FCSTD DOCUMENT  (FreeCAD 0.19R0.19.2)
Label: boatMoterHolder001
License: All rights reserved
LicenseURL: http://en.wikipedia.org/wiki/All_rights_reserved
objects: Sketcher::SketchObject×1
note: 1 computed .brp shape members not serialized (recipe doc carries the construction recipe); baked Part::Feature solids carry a one-line shape summary decoded from their .brp

FEATURE [Sketcher::SketchObject] Sketch
  FullyConstrained = true
  sketch-geometry (12):
    g0: Circle CenterX=-6 CenterY=0 CenterZ=0 NormalX=0 NormalY=0 NormalZ=1 AngleXU=0 Radius=0.9
    g1: Circle CenterX=0 CenterY=6 CenterZ=0 NormalX=0 NormalY=0 NormalZ=1 AngleXU=0 Radius=0.9
    g2: Circle CenterX=6 CenterY=0 CenterZ=0 NormalX=0 NormalY=0 NormalZ=1 AngleXU=0 Radius=0.9
    g3: Circle CenterX=0 CenterY=-6 CenterZ=0 NormalX=0 NormalY=0 NormalZ=1 AngleXU=0 Radius=0.9
    g4: LineSegment StartX=0 StartY=0 StartZ=0 EndX=3.53553 EndY=-3.53553 EndZ=0
    g5: LineSegment StartX=-3.53553 StartY=-3.53553 StartZ=0 EndX=4e-16 EndY=0 EndZ=0
    g6: LineSegment StartX=3.53553 StartY=3.53553 StartZ=0 EndX=0 EndY=0 EndZ=0
    g7: LineSegment StartX=0 StartY=0 StartZ=0 EndX=-3.53553 EndY=3.53553 EndZ=0
    g8: LineSegment StartX=-7.77817 StartY=7.77817 StartZ=0 EndX=-3.53553 EndY=3.53553 EndZ=0
    g9: LineSegment StartX=3.53553 StartY=-3.53553 StartZ=0 EndX=7.77817 EndY=-7.77817 EndZ=0
    g10: LineSegment StartX=3.53553 StartY=3.53553 StartZ=0 EndX=7.77817 EndY=7.77817 EndZ=0
    g11: LineSegment StartX=-3.53553 StartY=-3.53553 StartZ=0 EndX=-7.77817 EndY=-7.77817 EndZ=0
  constraints (28):
    c: Block(g1)
    c: Block(g2)
    c: Block(g3)
    c: Block(g0)
    c: Coincident(g4,g-1)
    c: Distance(g4) = 5
    c: Angle(g4,g-1) = 0.785398
    c: Equal(g4,g5) = 5
    c: Coincident(g5,g4)
    c: Angle(g6,g-1) = 2.35619
    c: Distance(g6) = 5
    c: Coincident(g6,g4)
    c: Angle(g-1,g5) = 3.92699
    c: Coincident(g7,g4)
    c: Angle(g7,g5) = 1.5708
    c: Distance(g7) = 5
    c: Coincident(g8,g7)
    c: Distance(g8) = 6
    c: Parallel(g7,g8)
    c: Coincident(g9,g4)
    c: Distance(g9) = 6
    c: Parallel(g9,g4)
    c: Coincident(g10,g6)
    c: Distance(g10) = 6
    c: Parallel(g10,g6)
    c: Coincident(g11,g5)
    c: Distance(g11) = 6
    c: Parallel(g11,g5)
